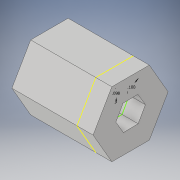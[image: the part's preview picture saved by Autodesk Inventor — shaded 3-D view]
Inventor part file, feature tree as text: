
AUTODESK INVENTOR PART (.ipt)
format: ipt  version: 2019 (Build 230136000, 136)  size: 119,296 bytes
history: native  units: in
note: dims shown in document units (in); Inventor stores cm internally (conversion verified against a paired STEP export)
features: extrude x3, sketch x2, projected_geometry x1
ambient origin geometry x8: Origin, YZ Plane, XZ Plane, XY Plane, X Axis, Y Axis, Z Axis, Center Point
bodies: Solid1 (feature_tree)
feature tree (6):
  extrude  "Extrusion1"  Depth=0.125in TaperAngle=0.0deg
  sketch  "Sketch3"  dims[d6=0.0984in d7=0.1in d8=0.5in d9=0.0in d10=0.5in d11=0.0in]
  extrude  "Extrusion3"  Depth=0.5in
  extrude  "Extrusion4"  Depth=0.5in TaperAngle=0.0deg
  sketch  "Sketch1"  dims[d0=0.25in d1=0.125in d2=0.0in]
  projected_geometry  "Projected Loop2"
